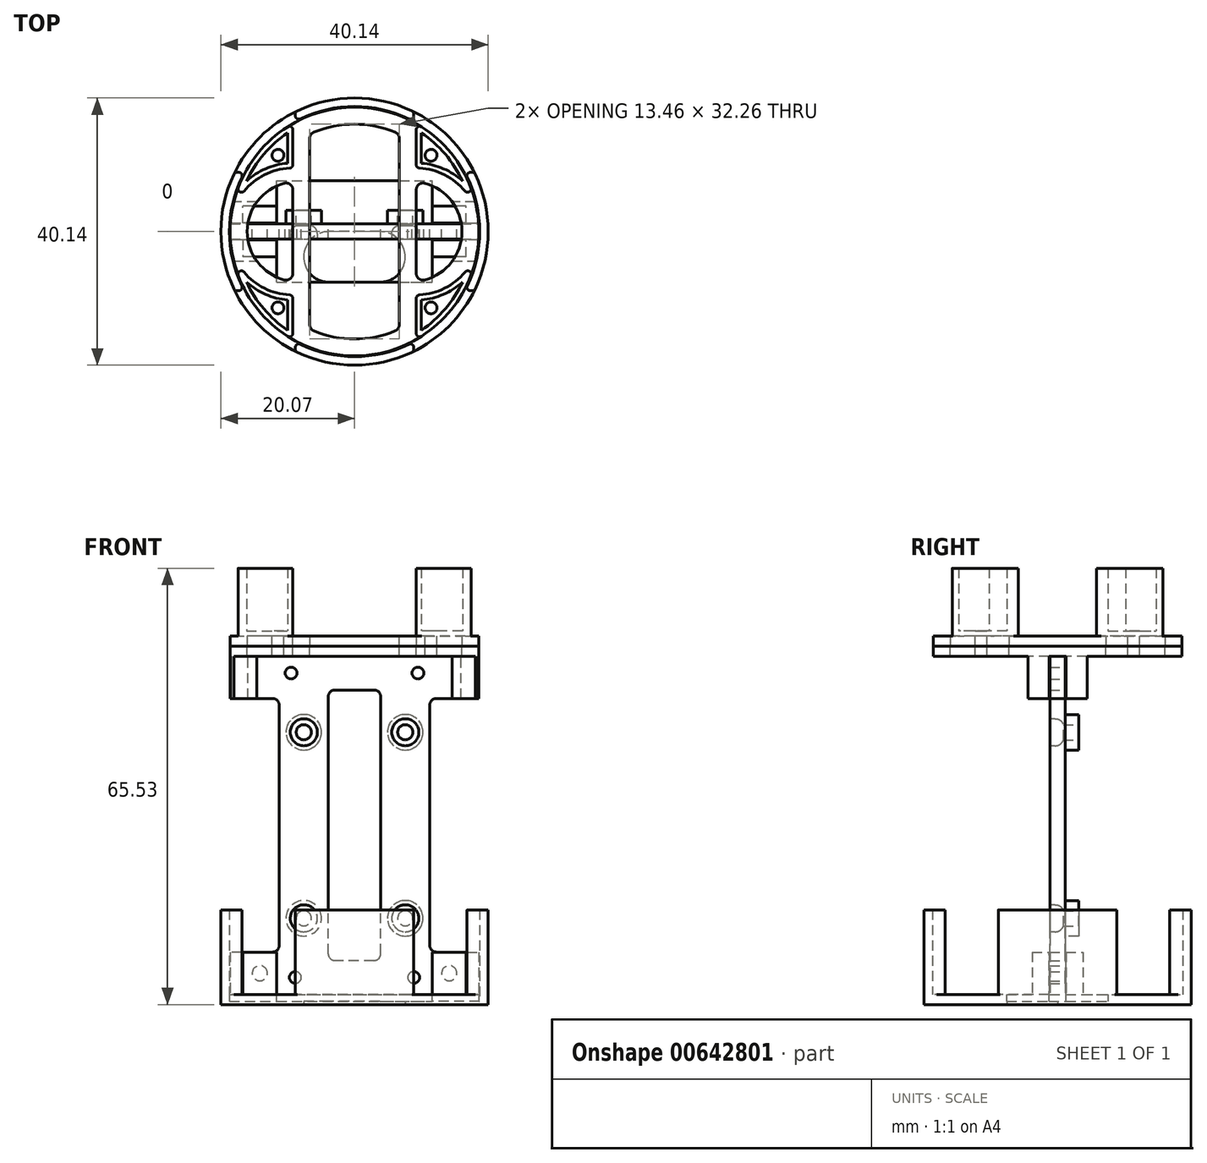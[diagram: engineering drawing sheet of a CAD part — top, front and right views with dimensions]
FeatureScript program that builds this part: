
annotation { "Feature Type Name" : "Feature", "Feature Type Description" : "" }
export const myFeature = defineFeature(function(context is Context, id is Id, definition is map)
    precondition{}
    {
        {
            var Q0;
            Q0=qCreatedBy(makeId("Top.planeOp"),FACE);
            var sketch = newSketch(context, id + "F0", { "sketchPlane" : qUnion([Q0])});
            skCircle(sketch, "E0", {"center": v(0, 0) * mm, "radius": 18.67 * mm});
            skSolve(sketch);
        }
        {
            var Q0;
            Q0=qSketchRegion(id+"F0",true);
            extrude(context, id + "F1", {"entities" : qUnion([Q0]), "depth" : 1.52 * mm, "offsetDistance" : 25.4 * mm});
        }
        {
            var Q0;
            Q0=makeQuery(id+"F1.opExtrude","CAP_FACE",FACE,{"disambiguationData":[OSD([sQuery(id+"F0.wireOp",EDGE,"E0")])],"isStart":false});
            var sketch = newSketch(context, id + "F2", { "sketchPlane" : qUnion([Q0])});
            skLineSegment(sketch, "E1.bottom", {"start": v(-9.27, 9.53) * mm, "end": v(9.27, 9.53) * mm, "construction": true});
            skLineSegment(sketch, "E1.top", {"start": v(-9.27, -9.53) * mm, "end": v(9.27, -9.53) * mm, "construction": true});
            skLineSegment(sketch, "E1.left", {"start": v(-9.27, 9.52) * mm, "end": v(-9.27, -9.53) * mm, "construction": true});
            skLineSegment(sketch, "E1.right", {"start": v(9.27, 9.53) * mm, "end": v(9.27, -9.53) * mm, "construction": true});
            skPoint(sketch, "E1.middle", {"position": v(0, 0) * mm});
            skArc(sketch, "E2", {"start": v(-9.27, 9.52) * mm, "mid": v(-15.18, 7.47) * mm, "end": v(-18.54, 2.2) * mm});
            skArc(sketch, "E3", {"start": v(9.27, -9.52) * mm, "mid": v(15.18, -7.47) * mm, "end": v(18.54, -2.2) * mm});
            skArc(sketch, "E4", {"start": v(-18.54, 2.2) * mm, "mid": v(-18.8, 0) * mm, "end": v(-18.54, -2.2) * mm, "construction": true});
            skArc(sketch, "E5", {"start": v(-18.54, 2.2) * mm, "mid": v(-18.67, 0) * mm, "end": v(-18.54, -2.2) * mm, "construction": true});
            skArc(sketch, "E6", {"start": v(-18.54, -2.2) * mm, "mid": v(0, -18.67) * mm, "end": v(18.54, -2.2) * mm});
            skArc(sketch, "E7", {"start": v(-18.54, -2.2) * mm, "mid": v(-15.18, -7.47) * mm, "end": v(-9.27, -9.53) * mm});
            skArc(sketch, "E8", {"start": v(18.54, 2.2) * mm, "mid": v(15.18, 7.47) * mm, "end": v(9.27, 9.53) * mm});
            skLineSegment(sketch, "E9", {"start": v(18.54, -2.2) * mm, "end": v(18.54, -2.2) * mm});
            skArc(sketch, "E10", {"start": v(18.54, -2.2) * mm, "mid": v(18.8, 0) * mm, "end": v(18.54, 2.2) * mm, "construction": true});
            skLineSegment(sketch, "E11", {"start": v(18.54, 2.2) * mm, "end": v(18.54, 2.2) * mm});
            skArc(sketch, "E12", {"start": v(18.54, 2.2) * mm, "mid": v(0, 18.67) * mm, "end": v(-18.54, 2.2) * mm});
            skArc(sketch, "E13", {"start": v(18.54, -2.2) * mm, "mid": v(18.67, 0) * mm, "end": v(18.54, 2.2) * mm, "construction": true});
            skLineSegment(sketch, "E14", {"start": v(-9.27, -9.53) * mm, "end": v(-9.27, -16.2) * mm});
            skLineSegment(sketch, "E15", {"start": v(9.27, -9.53) * mm, "end": v(9.27, -16.2) * mm});
            skLineSegment(sketch, "E16", {"start": v(9.27, 9.53) * mm, "end": v(9.27, 16.2) * mm});
            skLineSegment(sketch, "E17", {"start": v(-9.27, 9.53) * mm, "end": v(-9.27, 16.2) * mm});
            skArc(sketch, "E18", {"start": v(9.27, 16.2) * mm, "mid": v(0, 18.67) * mm, "end": v(-9.27, 16.2) * mm});
            skArc(sketch, "E19", {"start": v(-9.27, -16.2) * mm, "mid": v(0, -18.67) * mm, "end": v(9.27, -16.2) * mm});
            skSolve(sketch);
        }
        {
            var Q0;
            Q0=qSketchRegion(id+"F2",true);
            extrude(context, id + "F3", {"entities" : qUnion([Q0]), "operationType" : NewBodyOperationType.ADD, "depth" : 10.16 * mm, "offsetDistance" : 25.4 * mm});
        }
        {
            var Q0;
            Q0=makeQuery(id+"F3.opExtrude","SWEPT_EDGE",EDGE,{"disambiguationData":[OSD([sQuery(id+"F0.wireOp",EDGE,"E0"),sQuery(id+"F2.wireOp",EDGE,"E2"),sQuery(id+"F2.wireOp",EDGE,"E12")])]});
            var Q1;
            Q1=makeQuery(id+"F3.opExtrude","SWEPT_EDGE",EDGE,{"disambiguationData":[OSD([sQuery(id+"F0.wireOp",EDGE,"E0"),sQuery(id+"F2.wireOp",EDGE,"E6"),sQuery(id+"F2.wireOp",EDGE,"E7")])]});
            var Q2;
            Q2=makeQuery(id+"F3.opExtrude","SWEPT_EDGE",EDGE,{"disambiguationData":[OSD([sQuery(id+"F0.wireOp",EDGE,"E0"),sQuery(id+"F2.wireOp",EDGE,"E8"),sQuery(id+"F2.wireOp",EDGE,"E12")])]});
            var Q3;
            Q3=makeQuery(id+"F3.opExtrude","SWEPT_EDGE",EDGE,{"disambiguationData":[OSD([sQuery(id+"F0.wireOp",EDGE,"E0"),sQuery(id+"F2.wireOp",EDGE,"E3"),sQuery(id+"F2.wireOp",EDGE,"E6")])]});
            var Q4;
            Q4=makeQuery(id+"F3.opExtrude","SWEPT_EDGE",EDGE,{"disambiguationData":[OSD([sQuery(id+"F2.wireOp",EDGE,"E6"),sQuery(id+"F2.wireOp",EDGE,"E14"),sQuery(id+"F2.wireOp",EDGE,"E19")])]});
            var Q5;
            Q5=makeQuery(id+"F3.opExtrude","SWEPT_EDGE",EDGE,{"disambiguationData":[OSD([sQuery(id+"F0.wireOp",EDGE,"RRU1Pf1V-DoVO-Xhje-gmtz-4FpblWX3eckG.bottom"),sQuery(id+"F0.wireOp",EDGE,"RRU1Pf1V-DoVO-Xhje-gmtz-4FpblWX3eckG.left"),sQuery(id+"F2.wireOp",EDGE,"E7"),sQuery(id+"F2.wireOp",EDGE,"E14")])]});
            var Q6;
            Q6=makeQuery(id+"F3.opExtrude","SWEPT_EDGE",EDGE,{"disambiguationData":[OSD([sQuery(id+"F0.wireOp",EDGE,"RRU1Pf1V-DoVO-Xhje-gmtz-4FpblWX3eckG.top"),sQuery(id+"F0.wireOp",EDGE,"RRU1Pf1V-DoVO-Xhje-gmtz-4FpblWX3eckG.left"),sQuery(id+"F2.wireOp",EDGE,"E2"),sQuery(id+"F2.wireOp",EDGE,"E17")])]});
            var Q7;
            Q7=makeQuery(id+"F3.opExtrude","SWEPT_EDGE",EDGE,{"disambiguationData":[OSD([sQuery(id+"F2.wireOp",EDGE,"E12"),sQuery(id+"F2.wireOp",EDGE,"E17"),sQuery(id+"F2.wireOp",EDGE,"E18")])]});
            var Q8;
            Q8=makeQuery(id+"F3.opExtrude","SWEPT_EDGE",EDGE,{"disambiguationData":[OSD([sQuery(id+"F2.wireOp",EDGE,"E12"),sQuery(id+"F2.wireOp",EDGE,"E16"),sQuery(id+"F2.wireOp",EDGE,"E18")])]});
            var Q9;
            Q9=makeQuery(id+"F3.opExtrude","SWEPT_EDGE",EDGE,{"disambiguationData":[OSD([sQuery(id+"F2.wireOp",EDGE,"E6"),sQuery(id+"F2.wireOp",EDGE,"E15"),sQuery(id+"F2.wireOp",EDGE,"E19")])]});
            var Q10;
            Q10=makeQuery(id+"F3.opExtrude","SWEPT_EDGE",EDGE,{"disambiguationData":[OSD([sQuery(id+"F0.wireOp",EDGE,"RRU1Pf1V-DoVO-Xhje-gmtz-4FpblWX3eckG.top"),sQuery(id+"F0.wireOp",EDGE,"RRU1Pf1V-DoVO-Xhje-gmtz-4FpblWX3eckG.right"),sQuery(id+"F2.wireOp",EDGE,"E8"),sQuery(id+"F2.wireOp",EDGE,"E16")])]});
            var Q11;
            Q11=makeQuery(id+"F3.opExtrude","SWEPT_EDGE",EDGE,{"disambiguationData":[OSD([sQuery(id+"F0.wireOp",EDGE,"RRU1Pf1V-DoVO-Xhje-gmtz-4FpblWX3eckG.bottom"),sQuery(id+"F0.wireOp",EDGE,"RRU1Pf1V-DoVO-Xhje-gmtz-4FpblWX3eckG.right"),sQuery(id+"F2.wireOp",EDGE,"E3"),sQuery(id+"F2.wireOp",EDGE,"E15")])]});
            fillet(context, id + "F4", {"entities" : qUnion([Q0, Q1, Q2, Q3, Q4, Q5, Q6, Q7, Q8, Q9, Q10, Q11]), "radius" : 0.5 * mm, "tangentPropagation" : true, "allowEdgeOverflow" : false});
        }
        {
            var Q0;
            Q0=makeQuery(id+"F3.opExtrude","CAP_FACE",FACE,{"disambiguationData":[OSD([sQuery(id+"F2.wireOp",EDGE,"E1.bottom"),sQuery(id+"F2.wireOp",EDGE,"E2"),sQuery(id+"F2.wireOp",EDGE,"E8"),sQuery(id+"F2.wireOp",EDGE,"E12")])],"isStart":false});
            var Q1;
            Q1=makeQuery(id+"F3.opExtrude","CAP_FACE",FACE,{"disambiguationData":[OSD([sQuery(id+"F2.wireOp",EDGE,"E1.top"),sQuery(id+"F2.wireOp",EDGE,"E3"),sQuery(id+"F2.wireOp",EDGE,"E6"),sQuery(id+"F2.wireOp",EDGE,"E7")])],"isStart":false});
            shell(context, id + "F5", {"entities" : qUnion([Q0, Q1]), "thickness" : 0.76 * mm});
        }
        {
            var Q0;
            Q0=makeQuery(id+"F1.opExtrude","CAP_FACE",FACE,{"disambiguationData":[OSD([sQuery(id+"F0.wireOp",EDGE,"E0")])],"isStart":true});
            var sketch = newSketch(context, id + "F6", { "sketchPlane" : qUnion([Q0])});
            skLineSegment(sketch, "E20.bottom", {"start": v(6.73, -14.66) * mm, "end": v(-6.73, -14.66) * mm, "construction": true});
            skLineSegment(sketch, "E20.top", {"start": v(6.73, 14.66) * mm, "end": v(-6.73, 14.66) * mm, "construction": true});
            skLineSegment(sketch, "E20.left", {"start": v(6.73, -14.66) * mm, "end": v(6.73, 14.66) * mm});
            skLineSegment(sketch, "E20.right", {"start": v(-6.73, -14.66) * mm, "end": v(-6.73, 14.66) * mm});
            skPoint(sketch, "E20.middle", {"position": v(0, 0) * mm});
            skArc(sketch, "E21", {"start": v(-6.73, -14.66) * mm, "mid": v(0, -16.13) * mm, "end": v(6.73, -14.66) * mm});
            skArc(sketch, "E22", {"start": v(6.73, 14.66) * mm, "mid": v(0, 16.13) * mm, "end": v(-6.73, 14.66) * mm});
            skLineSegment(sketch, "E23", {"start": v(0, -16.13) * mm, "end": v(0, -18.67) * mm, "construction": true});
            skLineSegment(sketch, "E24", {"start": v(6.73, -14.66) * mm, "end": v(9.27, -14.66) * mm, "construction": true});
            skLineSegment(sketch, "E25", {"start": v(9.27, -7.48) * mm, "end": v(9.27, 7.48) * mm});
            skPoint(sketch, "E26", {"position": v(9.27, 0) * mm});
            skArc(sketch, "E27", {"start": v(9.27, -7.48) * mm, "mid": v(16.13, 0) * mm, "end": v(9.27, 7.48) * mm});
            skLineSegment(sketch, "E28", {"start": v(16.13, 0) * mm, "end": v(18.67, 0) * mm, "construction": true});
            skLineSegment(sketch, "E29", {"start": v(9.27, -7.48) * mm, "end": v(9.27, -10.02) * mm, "construction": true});
            skLineSegment(sketch, "E30", {"start": v(-9.27, -7.48) * mm, "end": v(-9.27, 7.48) * mm});
            skArc(sketch, "E31", {"start": v(-9.27, 7.48) * mm, "mid": v(-16.13, 0) * mm, "end": v(-9.27, -7.48) * mm});
            skLineSegment(sketch, "E32", {"start": v(-16.13, 0) * mm, "end": v(-18.67, 0) * mm, "construction": true});
            skSolve(sketch);
        }
        {
            var Q0;
            Q0=qSketchRegion(id+"F6",true);
            var Q1;
            Q1=makeQuery(id+"F1.opExtrude","CAP_FACE",FACE,{"disambiguationData":[OSD([sQuery(id+"F0.wireOp",EDGE,"E0")])],"isStart":false});
            extrude(context, id + "F7", {"entities" : qUnion([Q0]), "operationType" : NewBodyOperationType.REMOVE, "endBound" : BoundingType.UP_TO_SURFACE, "oppositeDirection" : true, "depth" : 25.4 * mm, "endBoundEntityFace" : qUnion([Q1]), "offsetDistance" : 25.4 * mm});
        }
        {
            var Q0;
            Q0=makeQuery(id+"F3.opExtrude","CAP_EDGE",EDGE,{"disambiguationData":[OSD([sQuery(id+"F2.wireOp",EDGE,"E2")])],"isStart":true});
            var Q1;
            Q1=makeQuery(id+"F3.opExtrude","CAP_EDGE",EDGE,{"disambiguationData":[OSD([sQuery(id+"F2.wireOp",EDGE,"E7")])],"isStart":true});
            var Q2;
            Q2=makeQuery(id+"F3.opExtrude","CAP_EDGE",EDGE,{"disambiguationData":[OSD([sQuery(id+"F2.wireOp",EDGE,"E3")])],"isStart":true});
            var Q3;
            Q3=makeQuery(id+"F3.opExtrude","CAP_EDGE",EDGE,{"disambiguationData":[OSD([sQuery(id+"F2.wireOp",EDGE,"E8")])],"isStart":true});
            var Q4;
            {var subQ0=sQuery(id+"F6.wireOp",EDGE,"E31");var subQ1=sQuery(id+"F6.wireOp",EDGE,"E30");Q4=makeQuery(id+"F7.boolean.opBoolean","COPY",EDGE,{"derivedFrom":makeQuery(id+"F7.opExtrude","SWEPT_EDGE",EDGE,{"disambiguationData":[OSD([subQ1,subQ0]),TDD([makeQuery(id+"F6.imprint","INTERSECT",VERTEX,{"disambiguationData":[OD(0.0)],"derivedFrom":[subQ1,subQ0]})])]})});}
            var Q5;
            Q5=makeQuery(id+"F7.boolean.opBoolean","COPY",EDGE,{"derivedFrom":makeQuery(id+"F7.opExtrude","SWEPT_EDGE",EDGE,{"disambiguationData":[OSD([sQuery(id+"F6.wireOp",EDGE,"E20.right"),sQuery(id+"F6.wireOp",EDGE,"E21")])]})});
            var Q6;
            Q6=makeQuery(id+"F7.boolean.opBoolean","COPY",EDGE,{"derivedFrom":makeQuery(id+"F7.opExtrude","SWEPT_EDGE",EDGE,{"disambiguationData":[OSD([sQuery(id+"F6.wireOp",EDGE,"E20.left"),sQuery(id+"F6.wireOp",EDGE,"E21")])]})});
            var Q7;
            {var subQ0=sQuery(id+"F6.wireOp",EDGE,"E31");var subQ1=sQuery(id+"F6.wireOp",EDGE,"E30");Q7=makeQuery(id+"F7.boolean.opBoolean","COPY",EDGE,{"derivedFrom":makeQuery(id+"F7.opExtrude","SWEPT_EDGE",EDGE,{"disambiguationData":[OSD([subQ1,subQ0]),TDD([makeQuery(id+"F6.imprint","INTERSECT",VERTEX,{"disambiguationData":[OD(1.0)],"derivedFrom":[subQ1,subQ0]})])]})});}
            var Q8;
            Q8=makeQuery(id+"F7.boolean.opBoolean","COPY",EDGE,{"derivedFrom":makeQuery(id+"F7.opExtrude","SWEPT_EDGE",EDGE,{"disambiguationData":[OSD([sQuery(id+"F6.wireOp",EDGE,"E20.left"),sQuery(id+"F6.wireOp",EDGE,"E22")])]})});
            var Q9;
            {var subQ0=sQuery(id+"F6.wireOp",EDGE,"E27");var subQ1=sQuery(id+"F6.wireOp",EDGE,"E25");Q9=makeQuery(id+"F7.boolean.opBoolean","COPY",EDGE,{"derivedFrom":makeQuery(id+"F7.opExtrude","SWEPT_EDGE",EDGE,{"disambiguationData":[OSD([subQ1,subQ0]),TDD([makeQuery(id+"F6.imprint","INTERSECT",VERTEX,{"disambiguationData":[OD(1.0)],"derivedFrom":[subQ1,subQ0]})])]})});}
            var Q10;
            Q10=makeQuery(id+"F7.boolean.opBoolean","COPY",EDGE,{"derivedFrom":makeQuery(id+"F7.opExtrude","SWEPT_EDGE",EDGE,{"disambiguationData":[OSD([sQuery(id+"F6.wireOp",EDGE,"E20.right"),sQuery(id+"F6.wireOp",EDGE,"E22")])]})});
            var Q11;
            {var subQ0=sQuery(id+"F6.wireOp",EDGE,"E27");var subQ1=sQuery(id+"F6.wireOp",EDGE,"E25");Q11=makeQuery(id+"F7.boolean.opBoolean","COPY",EDGE,{"derivedFrom":makeQuery(id+"F7.opExtrude","SWEPT_EDGE",EDGE,{"disambiguationData":[OSD([subQ1,subQ0]),TDD([makeQuery(id+"F6.imprint","INTERSECT",VERTEX,{"disambiguationData":[OD(0.0)],"derivedFrom":[subQ1,subQ0]})])]})});}
            fillet(context, id + "F8", {"entities" : qUnion([Q0, Q1, Q2, Q3, Q4, Q5, Q6, Q7, Q8, Q9, Q10, Q11]), "radius" : 1.02 * mm, "tangentPropagation" : true, "allowEdgeOverflow" : false});
        }
        {
            var Q0;
            Q0=makeQuery(id+"F5.opShell","OFFSET_FACE",FACE,{"disambiguationData":[OSD([sQuery(id+"F0.wireOp",EDGE,"E0")]),OD(0.0)]});
            var sketch = newSketch(context, id + "F9", { "sketchPlane" : qUnion([Q0])});
            skCircle(sketch, "E33", {"center": v(-11.5, 11.46) * mm, "radius": 0.89 * mm});
            skLineSegment(sketch, "E34.bottom", {"start": v(-11.5, 11.46) * mm, "end": v(11.5, 11.46) * mm, "construction": true});
            skLineSegment(sketch, "E34.top", {"start": v(-11.5, -11.46) * mm, "end": v(11.5, -11.46) * mm, "construction": true});
            skLineSegment(sketch, "E34.left", {"start": v(-11.5, 11.46) * mm, "end": v(-11.5, -11.46) * mm, "construction": true});
            skLineSegment(sketch, "E34.right", {"start": v(11.5, 11.46) * mm, "end": v(11.5, -11.46) * mm, "construction": true});
            skPoint(sketch, "E34.middle", {"position": v(0, 0) * mm});
            skCircle(sketch, "E35", {"center": v(11.5, 11.46) * mm, "radius": 0.89 * mm});
            skCircle(sketch, "E36", {"center": v(11.5, -11.46) * mm, "radius": 0.89 * mm});
            skCircle(sketch, "E37", {"center": v(-11.5, -11.46) * mm, "radius": 0.89 * mm});
            skSolve(sketch);
        }
        {
            var Q0;
            Q0 = qSketchRegion(id + "F9", true);
            var Q1;
            Q1=makeQuery(id+"F1.opExtrude","CAP_FACE",FACE,{"disambiguationData":[OSD([sQuery(id+"F0.wireOp",EDGE,"E0")])],"isStart":true});
            extrude(context, id + "F10", {"entities" : qUnion([Q0]), "operationType" : NewBodyOperationType.REMOVE, "endBound" : BoundingType.UP_TO_SURFACE, "oppositeDirection" : true, "depth" : 25.4 * mm, "endBoundEntityFace" : qUnion([Q1]), "offsetDistance" : 25.4 * mm});
        }
        {
            var Q0;
            Q0=makeQuery(id+"F5.opShell","OFFSET_FACE",FACE,{"disambiguationData":[OSD([sQuery(id+"F0.wireOp",EDGE,"E0")]),OD(2.0)]});
            var Q1;
            Q1=makeQuery(id+"F5.opShell","OFFSET_FACE",FACE,{"disambiguationData":[OSD([sQuery(id+"F0.wireOp",EDGE,"E0")]),OD(1.0)]});
            var Q2;
            Q2=makeQuery(id+"F5.opShell","OFFSET_FACE",FACE,{"disambiguationData":[OSD([sQuery(id+"F0.wireOp",EDGE,"E0")]),OD(3.0)]});
            var Q3;
            Q3=makeQuery(id+"F5.opShell","OFFSET_FACE",FACE,{"disambiguationData":[OSD([sQuery(id+"F0.wireOp",EDGE,"E0")]),OD(0.0)]});
            extrude(context, id + "F11", {"entities" : qUnion([Q0, Q1, Q2, Q3]), "operationType" : NewBodyOperationType.ADD, "depth" : 1.52 * mm, "offsetDistance" : 25.4 * mm});
        }
        {
            var Q0;
            Q0=makeQuery(id+"F1.opExtrude","CAP_FACE",FACE,{"disambiguationData":[OSD([sQuery(id+"F0.wireOp",EDGE,"E0")])],"isStart":true});
            extrude(context, id + "F12", {"entities" : qUnion([Q0]), "depth" : 7.87 * mm, "offsetDistance" : 25.4 * mm});
        }
        {
            var Q0;
            Q0=makeQuery(id+"F12.opExtrude","CAP_FACE",FACE,{"disambiguationData":[OSD([sQuery(id+"F0.wireOp",EDGE,"E0")])],"isStart":false});
            var sketch = newSketch(context, id + "F13", { "sketchPlane" : qUnion([Q0])});
            skArc(sketch, "E38", {"start": v(-18.13, 4.45) * mm, "mid": v(-18.45, 2.87) * mm, "end": v(-18.63, 1.27) * mm, "construction": true});
            skArc(sketch, "E39", {"start": v(-18.13, -4.45) * mm, "mid": v(0, -18.67) * mm, "end": v(18.13, -4.44) * mm});
            skArc(sketch, "E40", {"start": v(18.13, -4.44) * mm, "mid": v(18.45, -2.87) * mm, "end": v(18.63, -1.27) * mm, "construction": true});
            skArc(sketch, "E41", {"start": v(18.13, 4.44) * mm, "mid": v(0, 18.67) * mm, "end": v(-18.13, 4.45) * mm});
            skLineSegment(sketch, "E42", {"start": v(-18.13, 4.45) * mm, "end": v(-9.27, 4.45) * mm});
            skLineSegment(sketch, "E43", {"start": v(18.13, -4.45) * mm, "end": v(9.27, -4.45) * mm});
            skArc(sketch, "E44", {"start": v(-18.63, 1.27) * mm, "mid": v(-18.67, 0) * mm, "end": v(-18.63, -1.27) * mm});
            skArc(sketch, "E45", {"start": v(-18.63, -1.27) * mm, "mid": v(-18.45, -2.87) * mm, "end": v(-18.13, -4.45) * mm, "construction": true});
            skArc(sketch, "E46", {"start": v(18.63, -1.27) * mm, "mid": v(18.67, 0) * mm, "end": v(18.63, 1.27) * mm});
            skArc(sketch, "E47", {"start": v(18.63, 1.27) * mm, "mid": v(18.45, 2.87) * mm, "end": v(18.13, 4.44) * mm, "construction": true});
            skLineSegment(sketch, "E48", {"start": v(18.63, 1.27) * mm, "end": v(9.27, 1.27) * mm});
            skLineSegment(sketch, "E49", {"start": v(-18.63, -1.27) * mm, "end": v(-9.27, -1.27) * mm});
            skLineSegment(sketch, "E50", {"start": v(-9.27, 4.45) * mm, "end": v(9.27, 4.45) * mm, "construction": true});
            skLineSegment(sketch, "E51", {"start": v(-9.27, 1.27) * mm, "end": v(-18.63, 1.27) * mm});
            skLineSegment(sketch, "E52", {"start": v(-9.27, -1.27) * mm, "end": v(9.27, -1.27) * mm, "construction": true});
            skLineSegment(sketch, "E53", {"start": v(-9.27, -4.45) * mm, "end": v(-18.13, -4.45) * mm});
            skLineSegment(sketch, "E54", {"start": v(9.27, -4.45) * mm, "end": v(-9.27, -4.45) * mm, "construction": true});
            skLineSegment(sketch, "E55", {"start": v(9.27, -1.27) * mm, "end": v(18.63, -1.27) * mm});
            skLineSegment(sketch, "E56", {"start": v(9.27, 1.27) * mm, "end": v(-9.27, 1.27) * mm, "construction": true});
            skLineSegment(sketch, "E57", {"start": v(9.27, 4.45) * mm, "end": v(18.13, 4.45) * mm});
            skLineSegment(sketch, "E58", {"start": v(0, 1.27) * mm, "end": v(0, -1.27) * mm, "construction": true});
            skLineSegment(sketch, "E59", {"start": v(0, 4.45) * mm, "end": v(0, -4.45) * mm, "construction": true});
            skLineSegment(sketch, "E60", {"start": v(-9.27, 4.45) * mm, "end": v(-9.27, 1.27) * mm});
            skLineSegment(sketch, "E61", {"start": v(-9.27, -1.27) * mm, "end": v(-9.27, -4.45) * mm});
            skLineSegment(sketch, "E62", {"start": v(9.27, -4.45) * mm, "end": v(9.27, -1.27) * mm});
            skLineSegment(sketch, "E63", {"start": v(9.27, 1.27) * mm, "end": v(9.27, 4.45) * mm});
            skSolve(sketch);
        }
        {
            var Q0;
            Q0 = qSketchRegion(id + "F13", true);
            extrude(context, id + "F14", {"entities" : qUnion([Q0]), "operationType" : NewBodyOperationType.REMOVE, "oppositeDirection" : true, "depth" : 6.35 * mm, "offsetDistance" : 25.4 * mm});
        }
        {
            var Q0;
            Q0=qCreatedBy(makeId("Front.planeOp"),FACE);
            var sketch = newSketch(context, id + "F15", { "sketchPlane" : qUnion([Q0])});
            skLineSegment(sketch, "E64.bottom", {"start": v(-7.62, -40.9) * mm, "end": v(7.62, -40.9) * mm, "construction": true});
            skLineSegment(sketch, "E64.top", {"start": v(-7.62, -12.95) * mm, "end": v(7.62, -12.95) * mm, "construction": true});
            skLineSegment(sketch, "E64.left", {"start": v(-7.62, -40.9) * mm, "end": v(-7.62, -12.95) * mm, "construction": true});
            skLineSegment(sketch, "E64.right", {"start": v(7.62, -40.9) * mm, "end": v(7.62, -12.95) * mm, "construction": true});
            skPoint(sketch, "E64.middle", {"position": v(0, -26.92) * mm});
            skCircle(sketch, "E65", {"center": v(-7.62, -40.9) * mm, "radius": 1.14 * mm});
            skCircle(sketch, "E66", {"center": v(-7.62, -12.95) * mm, "radius": 1.14 * mm});
            skCircle(sketch, "E67", {"center": v(7.62, -12.95) * mm, "radius": 1.14 * mm});
            skCircle(sketch, "E68", {"center": v(7.62, -40.9) * mm, "radius": 1.14 * mm});
            skLineSegment(sketch, "E69", {"start": v(-8.89, -49.78) * mm, "end": v(8.89, -49.78) * mm, "construction": true});
            skLineSegment(sketch, "E70", {"start": v(-9.53, -4.06) * mm, "end": v(9.53, -4.06) * mm, "construction": true});
            skPoint(sketch, "E71", {"position": v(0, -49.78) * mm});
            skPoint(sketch, "E72", {"position": v(0, -4.06) * mm});
            skLineSegment(sketch, "E73", {"start": v(0, -49.78) * mm, "end": v(0, -4.06) * mm, "construction": true});
            skCircle(sketch, "E74", {"center": v(-8.89, -49.78) * mm, "radius": 0.89 * mm});
            skCircle(sketch, "E75", {"center": v(8.89, -49.78) * mm, "radius": 0.89 * mm});
            skCircle(sketch, "E76", {"center": v(9.53, -4.06) * mm, "radius": 0.89 * mm});
            skCircle(sketch, "E77", {"center": v(-9.53, -4.06) * mm, "radius": 0.89 * mm});
            skLineSegment(sketch, "E78", {"start": v(-18.67, -52.32) * mm, "end": v(18.67, -52.32) * mm});
            skPoint(sketch, "E79", {"position": v(0, -52.32) * mm});
            skLineSegment(sketch, "E80", {"start": v(-18.67, -1.52) * mm, "end": v(18.67, -1.52) * mm});
            skLineSegment(sketch, "E81", {"start": v(9.52, -4.06) * mm, "end": v(9.52, -1.52) * mm, "construction": true});
            skLineSegment(sketch, "E82", {"start": v(8.9, -49.78) * mm, "end": v(8.9, -52.32) * mm, "construction": true});
            skLineSegment(sketch, "E83", {"start": v(-18.67, -1.52) * mm, "end": v(-18.67, -7.87) * mm});
            skLineSegment(sketch, "E84", {"start": v(-18.67, -7.87) * mm, "end": v(-11.3, -7.87) * mm});
            skLineSegment(sketch, "E85", {"start": v(-11.3, -7.87) * mm, "end": v(-11.3, -45.97) * mm});
            skLineSegment(sketch, "E86", {"start": v(-11.3, -45.97) * mm, "end": v(-18.67, -45.97) * mm});
            skLineSegment(sketch, "E87", {"start": v(-18.67, -45.97) * mm, "end": v(-18.67, -52.32) * mm});
            skLineSegment(sketch, "E88", {"start": v(18.67, -1.52) * mm, "end": v(18.67, -7.87) * mm});
            skLineSegment(sketch, "E89", {"start": v(18.67, -7.87) * mm, "end": v(11.3, -7.87) * mm});
            skLineSegment(sketch, "E90", {"start": v(11.3, -7.87) * mm, "end": v(11.3, -45.97) * mm});
            skLineSegment(sketch, "E91", {"start": v(11.3, -45.97) * mm, "end": v(18.67, -45.97) * mm});
            skLineSegment(sketch, "E92", {"start": v(18.67, -45.97) * mm, "end": v(18.67, -52.32) * mm});
            skLineSegment(sketch, "E93", {"start": v(-8.76, -40.9) * mm, "end": v(-11.3, -40.9) * mm, "construction": true});
            skLineSegment(sketch, "E94.bottom", {"start": v(3.94, -47.24) * mm, "end": v(-3.94, -47.24) * mm});
            skLineSegment(sketch, "E94.top", {"start": v(3.94, -6.6) * mm, "end": v(-3.94, -6.6) * mm});
            skLineSegment(sketch, "E94.left", {"start": v(3.94, -47.24) * mm, "end": v(3.94, -6.6) * mm});
            skLineSegment(sketch, "E94.right", {"start": v(-3.94, -47.24) * mm, "end": v(-3.94, -6.6) * mm});
            skLineSegment(sketch, "E95", {"start": v(-6.48, -40.9) * mm, "end": v(-3.94, -40.9) * mm, "construction": true});
            skLineSegment(sketch, "E96", {"start": v(0, -49.78) * mm, "end": v(0, -47.24) * mm, "construction": true});
            skCircle(sketch, "E97", {"center": v(-14.22, -49.15) * mm, "radius": 1.14 * mm});
            skPoint(sketch, "E97.centerSnap0", {"position": v(-18.67, -49.15) * mm});
            skCircle(sketch, "E98", {"center": v(14.22, -49.15) * mm, "radius": 1.14 * mm});
            skPoint(sketch, "E98.centerSnap0", {"position": v(18.67, -49.15) * mm});
            skLineSegment(sketch, "E99", {"start": v(-14.22, -49.15) * mm, "end": v(-18.67, -49.15) * mm, "construction": true});
            skLineSegment(sketch, "E100", {"start": v(14.22, -49.15) * mm, "end": v(18.67, -49.15) * mm, "construction": true});
            skSolve(sketch);
        }
        {
            var Q0;
            Q0 = qSketchRegion(id + "F15", true);
            extrude(context, id + "F16", {"entities" : qUnion([Q0]), "endBound" : BoundingType.SYMMETRIC, "depth" : 2.3 * mm, "offsetDistance" : 25.4 * mm});
        }
        {
            var Q0;
            Q0=makeQuery(id+"F16.opExtrude","CAP_FACE",FACE,{"disambiguationData":[OSD([sQuery(id+"F15.wireOp",EDGE,"E65"),sQuery(id+"F15.wireOp",EDGE,"E66"),sQuery(id+"F15.wireOp",EDGE,"E67"),sQuery(id+"F15.wireOp",EDGE,"E68"),sQuery(id+"F15.wireOp",EDGE,"E74"),sQuery(id+"F15.wireOp",EDGE,"E75"),sQuery(id+"F15.wireOp",EDGE,"E76"),sQuery(id+"F15.wireOp",EDGE,"E77"),sQuery(id+"F15.wireOp",EDGE,"E78"),sQuery(id+"F15.wireOp",EDGE,"E80"),sQuery(id+"F15.wireOp",EDGE,"E83"),sQuery(id+"F15.wireOp",EDGE,"E84"),sQuery(id+"F15.wireOp",EDGE,"E85"),sQuery(id+"F15.wireOp",EDGE,"E86"),sQuery(id+"F15.wireOp",EDGE,"E87"),sQuery(id+"F15.wireOp",EDGE,"E88"),sQuery(id+"F15.wireOp",EDGE,"E89"),sQuery(id+"F15.wireOp",EDGE,"E90"),sQuery(id+"F15.wireOp",EDGE,"E91"),sQuery(id+"F15.wireOp",EDGE,"E92"),sQuery(id+"F15.wireOp",EDGE,"E94.bottom"),sQuery(id+"F15.wireOp",EDGE,"E94.top"),sQuery(id+"F15.wireOp",EDGE,"E94.left"),sQuery(id+"F15.wireOp",EDGE,"E94.right")])],"isStart":true});
            var sketch = newSketch(context, id + "F17", { "sketchPlane" : qUnion([Q0])});
            skCircle(sketch, "E101", {"center": v(7.62, -40.9) * mm, "radius": 1.14 * mm});
            skCircle(sketch, "E102", {"center": v(-7.62, -40.9) * mm, "radius": 1.14 * mm});
            skCircle(sketch, "E103", {"center": v(-7.62, -12.95) * mm, "radius": 1.14 * mm});
            skCircle(sketch, "E104", {"center": v(7.62, -12.95) * mm, "radius": 1.14 * mm});
            skCircle(sketch, "E105", {"center": v(7.62, -40.9) * mm, "radius": 2.67 * mm});
            skCircle(sketch, "E106", {"center": v(-7.62, -40.9) * mm, "radius": 2.67 * mm});
            skCircle(sketch, "E107", {"center": v(-7.62, -12.95) * mm, "radius": 2.67 * mm});
            skCircle(sketch, "E108", {"center": v(7.62, -12.95) * mm, "radius": 2.67 * mm});
            skSolve(sketch);
        }
        {
            var Q0;
            Q0 = qSketchRegion(id + "F17", true);
            extrude(context, id + "F18", {"entities" : qUnion([Q0]), "operationType" : NewBodyOperationType.ADD, "depth" : 2.03 * mm, "offsetDistance" : 25.4 * mm});
        }
        {
            var Q0;
            Q0=makeQuery(id+"F18.opExtrude","CAP_EDGE",EDGE,{"disambiguationData":[OSD([sQuery(id+"F17.wireOp",EDGE,"E105")])],"isStart":true});
            var Q1;
            Q1=makeQuery(id+"F18.opExtrude","CAP_EDGE",EDGE,{"disambiguationData":[OSD([sQuery(id+"F17.wireOp",EDGE,"E106")])],"isStart":true});
            var Q2;
            Q2=makeQuery(id+"F18.opExtrude","CAP_EDGE",EDGE,{"disambiguationData":[OSD([sQuery(id+"F17.wireOp",EDGE,"E108")])],"isStart":true});
            var Q3;
            Q3=makeQuery(id+"F18.opExtrude","CAP_EDGE",EDGE,{"disambiguationData":[OSD([sQuery(id+"F17.wireOp",EDGE,"E107")])],"isStart":true});
            var Q4;
            Q4=makeQuery(id+"F16.opExtrude","SWEPT_EDGE",EDGE,{"disambiguationData":[OSD([sQuery(id+"F15.wireOp",EDGE,"E85"),sQuery(id+"F15.wireOp",EDGE,"E86")])]});
            var Q5;
            Q5=makeQuery(id+"F16.opExtrude","SWEPT_EDGE",EDGE,{"disambiguationData":[OSD([sQuery(id+"F15.wireOp",EDGE,"E94.bottom"),sQuery(id+"F15.wireOp",EDGE,"E94.left")])]});
            var Q6;
            Q6=makeQuery(id+"F16.opExtrude","SWEPT_EDGE",EDGE,{"disambiguationData":[OSD([sQuery(id+"F15.wireOp",EDGE,"E94.bottom"),sQuery(id+"F15.wireOp",EDGE,"E94.right")])]});
            var Q7;
            Q7=makeQuery(id+"F16.opExtrude","SWEPT_EDGE",EDGE,{"disambiguationData":[OSD([sQuery(id+"F15.wireOp",EDGE,"E90"),sQuery(id+"F15.wireOp",EDGE,"E91")])]});
            var Q8;
            Q8=makeQuery(id+"F16.opExtrude","SWEPT_EDGE",EDGE,{"disambiguationData":[OSD([sQuery(id+"F15.wireOp",EDGE,"E84"),sQuery(id+"F15.wireOp",EDGE,"E85")])]});
            var Q9;
            Q9=makeQuery(id+"F16.opExtrude","SWEPT_EDGE",EDGE,{"disambiguationData":[OSD([sQuery(id+"F15.wireOp",EDGE,"E94.top"),sQuery(id+"F15.wireOp",EDGE,"E94.left")])]});
            var Q10;
            Q10=makeQuery(id+"F16.opExtrude","SWEPT_EDGE",EDGE,{"disambiguationData":[OSD([sQuery(id+"F15.wireOp",EDGE,"E94.top"),sQuery(id+"F15.wireOp",EDGE,"E94.right")])]});
            var Q11;
            Q11=makeQuery(id+"F16.opExtrude","SWEPT_EDGE",EDGE,{"disambiguationData":[OSD([sQuery(id+"F15.wireOp",EDGE,"E89"),sQuery(id+"F15.wireOp",EDGE,"E90")])]});
            fillet(context, id + "F19", {"entities" : qUnion([Q0, Q1, Q2, Q3, Q4, Q5, Q6, Q7, Q8, Q9, Q10, Q11]), "radius" : 1.02 * mm, "tangentPropagation" : true, "allowEdgeOverflow" : false});
        }
        {
            var Q0;
            Q0=makeQuery(id+"F16.opExtrude","CAP_FACE",FACE,{"disambiguationData":[OSD([sQuery(id+"F15.wireOp",EDGE,"E65"),sQuery(id+"F15.wireOp",EDGE,"E66"),sQuery(id+"F15.wireOp",EDGE,"E67"),sQuery(id+"F15.wireOp",EDGE,"E68"),sQuery(id+"F15.wireOp",EDGE,"E74"),sQuery(id+"F15.wireOp",EDGE,"E75"),sQuery(id+"F15.wireOp",EDGE,"E76"),sQuery(id+"F15.wireOp",EDGE,"E77"),sQuery(id+"F15.wireOp",EDGE,"E78"),sQuery(id+"F15.wireOp",EDGE,"E80"),sQuery(id+"F15.wireOp",EDGE,"E83"),sQuery(id+"F15.wireOp",EDGE,"E84"),sQuery(id+"F15.wireOp",EDGE,"E85"),sQuery(id+"F15.wireOp",EDGE,"E86"),sQuery(id+"F15.wireOp",EDGE,"E87"),sQuery(id+"F15.wireOp",EDGE,"E88"),sQuery(id+"F15.wireOp",EDGE,"E89"),sQuery(id+"F15.wireOp",EDGE,"E90"),sQuery(id+"F15.wireOp",EDGE,"E91"),sQuery(id+"F15.wireOp",EDGE,"E92"),sQuery(id+"F15.wireOp",EDGE,"E94.bottom"),sQuery(id+"F15.wireOp",EDGE,"E94.top"),sQuery(id+"F15.wireOp",EDGE,"E94.left"),sQuery(id+"F15.wireOp",EDGE,"E94.right"),sQuery(id+"F15.wireOp",EDGE,"E97"),sQuery(id+"F15.wireOp",EDGE,"E98")])],"isStart":false});
            var sketch = newSketch(context, id + "F20", { "sketchPlane" : qUnion([Q0])});
            skCircle(sketch, "E109", {"center": v(-7.62, -40.9) * mm, "radius": 2.03 * mm});
            skCircle(sketch, "E110", {"center": v(-7.62, -12.95) * mm, "radius": 2.03 * mm});
            skCircle(sketch, "E111", {"center": v(7.62, -12.95) * mm, "radius": 2.03 * mm});
            skCircle(sketch, "E112", {"center": v(7.62, -40.9) * mm, "radius": 2.03 * mm});
            skSolve(sketch);
        }
        {
            var Q0;
            Q0 = qSketchRegion(id + "F20", true);
            extrude(context, id + "F21", {"entities" : qUnion([Q0]), "operationType" : NewBodyOperationType.REMOVE, "oppositeDirection" : true, "depth" : 2.03 * mm, "offsetDistance" : 25.4 * mm});
        }
        {
            var Q0;
            Q0=makeQuery(id+"F21.boolean.opBoolean","COPY",EDGE,{"derivedFrom":makeQuery(id+"F21.opExtrude","CAP_EDGE",EDGE,{"disambiguationData":[OSD([sQuery(id+"F20.wireOp",EDGE,"E109")])],"isStart":false})});
            var Q1;
            Q1=makeQuery(id+"F21.boolean.opBoolean","COPY",EDGE,{"derivedFrom":makeQuery(id+"F21.opExtrude","CAP_EDGE",EDGE,{"disambiguationData":[OSD([sQuery(id+"F20.wireOp",EDGE,"E110")])],"isStart":false})});
            var Q2;
            Q2=makeQuery(id+"F21.boolean.opBoolean","COPY",EDGE,{"derivedFrom":makeQuery(id+"F21.opExtrude","CAP_EDGE",EDGE,{"disambiguationData":[OSD([sQuery(id+"F20.wireOp",EDGE,"E111")])],"isStart":false})});
            var Q3;
            Q3=makeQuery(id+"F21.boolean.opBoolean","COPY",EDGE,{"derivedFrom":makeQuery(id+"F21.opExtrude","CAP_EDGE",EDGE,{"disambiguationData":[OSD([sQuery(id+"F20.wireOp",EDGE,"E112")])],"isStart":false})});
            fillet(context, id + "F22", {"entities" : qUnion([Q0, Q1, Q2, Q3]), "radius" : 1.27 * mm, "tangentPropagation" : true, "allowEdgeOverflow" : false});
        }
        {
            var Q0;
            Q0=makeQuery(id+"F16.opExtrude","SWEPT_FACE",FACE,{"disambiguationData":[OSD([sQuery(id+"F15.wireOp",EDGE,"E78")])]});
            var sketch = newSketch(context, id + "F23", { "sketchPlane" : qUnion([Q0])});
            skCircle(sketch, "E113", {"center": v(0, 0) * mm, "radius": 20.07 * mm});
            skSolve(sketch);
        }
        {
            var Q0;
            Q0 = qSketchRegion(id + "F23", true);
            extrude(context, id + "F24", {"entities" : qUnion([Q0]), "depth" : 1.52 * mm, "offsetDistance" : 25.4 * mm});
        }
        {
            var Q0;
            Q0=makeQuery(id+"F24.opExtrude","CAP_FACE",FACE,{"disambiguationData":[OSD([sQuery(id+"F23.wireOp",EDGE,"E113")])],"isStart":false});
            var sketch = newSketch(context, id + "F25", { "sketchPlane" : qUnion([Q0])});
            skLineSegment(sketch, "E114.bottom", {"start": v(3.8, 0) * mm, "end": v(-3.8, 0) * mm});
            skLineSegment(sketch, "E114.top", {"start": v(3.8, 7.62) * mm, "end": v(-3.8, 7.62) * mm});
            skLineSegment(sketch, "E114.left", {"start": v(3.8, 0) * mm, "end": v(3.8, 7.62) * mm});
            skLineSegment(sketch, "E114.right", {"start": v(-3.81, 0) * mm, "end": v(-3.81, 7.62) * mm});
            skArc(sketch, "E115", {"start": v(3.81, 0) * mm, "mid": v(7.62, 3.81) * mm, "end": v(3.8, 7.62) * mm});
            skArc(sketch, "E116", {"start": v(-3.81, 7.62) * mm, "mid": v(-7.62, 3.81) * mm, "end": v(-3.81, 0) * mm});
            skPoint(sketch, "E117", {"position": v(0, 0) * mm});
            skSolve(sketch);
        }
        {
            var Q0;
            Q0 = qSketchRegion(id + "F25", true);
            var Q1;
            Q1=makeQuery(id+"F24.opExtrude","CAP_FACE",FACE,{"disambiguationData":[OSD([sQuery(id+"F23.wireOp",EDGE,"E113")])],"isStart":true});
            extrude(context, id + "F26", {"entities" : qUnion([Q0]), "operationType" : NewBodyOperationType.REMOVE, "endBound" : BoundingType.UP_TO_SURFACE, "oppositeDirection" : true, "depth" : 25.4 * mm, "endBoundEntityFace" : qUnion([Q1]), "offsetDistance" : 25.4 * mm});
        }
        {
            var Q0;
            Q0=makeQuery(id+"F24.opExtrude","CAP_FACE",FACE,{"disambiguationData":[OSD([sQuery(id+"F23.wireOp",EDGE,"E113")])],"isStart":true});
            var sketch = newSketch(context, id + "F27", { "sketchPlane" : qUnion([Q0])});
            skLineSegment(sketch, "E118.bottom", {"start": v(16.76, -3.8) * mm, "end": v(11.68, -3.81) * mm});
            skLineSegment(sketch, "E118.top", {"start": v(16.76, -1.27) * mm, "end": v(11.68, -1.27) * mm});
            skLineSegment(sketch, "E118.left", {"start": v(16.76, -3.81) * mm, "end": v(16.76, -1.27) * mm});
            skLineSegment(sketch, "E118.right", {"start": v(11.68, -3.8) * mm, "end": v(11.68, -1.27) * mm});
            skLineSegment(sketch, "E119.bottom", {"start": v(-11.68, 1.27) * mm, "end": v(-16.76, 1.27) * mm});
            skLineSegment(sketch, "E119.top", {"start": v(-11.68, 3.81) * mm, "end": v(-16.76, 3.81) * mm});
            skLineSegment(sketch, "E119.left", {"start": v(-11.68, 1.27) * mm, "end": v(-11.68, 3.81) * mm});
            skLineSegment(sketch, "E119.right", {"start": v(-16.76, 1.27) * mm, "end": v(-16.76, 3.81) * mm});
            skPoint(sketch, "E120", {"position": v(-14.22, 1.27) * mm});
            skPoint(sketch, "E121", {"position": v(-18.67, 1.14) * mm});
            skPoint(sketch, "E122", {"position": v(-20.07, 0) * mm});
            skPoint(sketch, "E123", {"position": v(20.07, 0) * mm});
            skPoint(sketch, "E124", {"position": v(18.67, -1.14) * mm});
            skPoint(sketch, "E125", {"position": v(14.22, -1.27) * mm});
            skLineSegment(sketch, "E126.bottom", {"start": v(16.76, 1.27) * mm, "end": v(11.68, 1.27) * mm});
            skLineSegment(sketch, "E126.top", {"start": v(16.76, 3.81) * mm, "end": v(11.68, 3.81) * mm});
            skLineSegment(sketch, "E126.left", {"start": v(16.76, 1.27) * mm, "end": v(16.76, 3.81) * mm});
            skLineSegment(sketch, "E126.right", {"start": v(11.68, 1.27) * mm, "end": v(11.68, 3.81) * mm});
            skLineSegment(sketch, "E127.bottom", {"start": v(-11.68, -1.27) * mm, "end": v(-16.76, -1.27) * mm});
            skLineSegment(sketch, "E127.top", {"start": v(-11.68, -3.8) * mm, "end": v(-16.76, -3.81) * mm});
            skLineSegment(sketch, "E127.left", {"start": v(-11.68, -1.27) * mm, "end": v(-11.68, -3.81) * mm});
            skLineSegment(sketch, "E127.right", {"start": v(-16.76, -1.27) * mm, "end": v(-16.76, -3.8) * mm});
            skSolve(sketch);
        }
        {
            var Q0;
            Q0=makeQuery(id+"F24.opExtrude","CAP_FACE",FACE,{"disambiguationData":[OSD([sQuery(id+"F23.wireOp",EDGE,"E113")])],"isStart":true});
            var sketch = newSketch(context, id + "F28", { "sketchPlane" : qUnion([Q0])});
            skLineSegment(sketch, "E128", {"start": v(0, -18.8) * mm, "end": v(0, -20.07) * mm, "construction": true});
            skArc(sketch, "E129", {"start": v(8.89, 17.99) * mm, "mid": v(0, 20.07) * mm, "end": v(-8.89, 17.99) * mm});
            skArc(sketch, "E130", {"start": v(-8.89, 17.99) * mm, "mid": v(-14.19, 14.19) * mm, "end": v(-17.99, 8.89) * mm, "construction": true});
            skArc(sketch, "E131", {"start": v(-8.9, 16.56) * mm, "mid": v(-13.3, 13.3) * mm, "end": v(-16.56, 8.89) * mm, "construction": true});
            skArc(sketch, "E132", {"start": v(8.9, 16.56) * mm, "mid": v(0, 18.8) * mm, "end": v(-8.9, 16.56) * mm});
            skArc(sketch, "E133", {"start": v(-8.9, -16.56) * mm, "mid": v(0, -18.8) * mm, "end": v(8.9, -16.56) * mm});
            skArc(sketch, "E134", {"start": v(8.9, -16.56) * mm, "mid": v(13.3, -13.3) * mm, "end": v(16.56, -8.89) * mm, "construction": true});
            skArc(sketch, "E135", {"start": v(8.89, -17.99) * mm, "mid": v(14.19, -14.19) * mm, "end": v(17.99, -8.89) * mm, "construction": true});
            skArc(sketch, "E136", {"start": v(-8.89, -17.99) * mm, "mid": v(0, -20.07) * mm, "end": v(8.89, -17.99) * mm});
            skLineSegment(sketch, "E137", {"start": v(8.89, 16.56) * mm, "end": v(8.89, 17.99) * mm});
            skLineSegment(sketch, "E138", {"start": v(-8.9, 17.99) * mm, "end": v(-8.9, 16.56) * mm});
            skLineSegment(sketch, "E139", {"start": v(-8.89, -16.56) * mm, "end": v(-8.89, -17.99) * mm});
            skLineSegment(sketch, "E140", {"start": v(8.89, -16.56) * mm, "end": v(8.9, -17.99) * mm});
            skArc(sketch, "E141", {"start": v(16.56, 8.89) * mm, "mid": v(13.3, 13.3) * mm, "end": v(8.9, 16.56) * mm, "construction": true});
            skArc(sketch, "E142", {"start": v(17.99, 8.89) * mm, "mid": v(14.19, 14.19) * mm, "end": v(8.89, 17.99) * mm, "construction": true});
            skArc(sketch, "E143", {"start": v(16.56, -8.89) * mm, "mid": v(18.8, 0) * mm, "end": v(16.56, 8.89) * mm});
            skArc(sketch, "E144", {"start": v(17.99, -8.89) * mm, "mid": v(20.07, 0) * mm, "end": v(17.99, 8.89) * mm});
            skArc(sketch, "E145", {"start": v(-16.56, 8.89) * mm, "mid": v(-18.8, 0) * mm, "end": v(-16.56, -8.89) * mm});
            skArc(sketch, "E146", {"start": v(-17.99, 8.89) * mm, "mid": v(-20.07, 0) * mm, "end": v(-17.99, -8.89) * mm});
            skArc(sketch, "E147", {"start": v(-16.56, -8.89) * mm, "mid": v(-13.3, -13.3) * mm, "end": v(-8.9, -16.56) * mm, "construction": true});
            skArc(sketch, "E148", {"start": v(-17.99, -8.89) * mm, "mid": v(-14.19, -14.19) * mm, "end": v(-8.89, -17.99) * mm, "construction": true});
            skLineSegment(sketch, "E149", {"start": v(-16.56, -8.9) * mm, "end": v(-17.99, -8.9) * mm});
            skLineSegment(sketch, "E150", {"start": v(-16.56, 8.89) * mm, "end": v(-17.99, 8.89) * mm});
            skLineSegment(sketch, "E151", {"start": v(17.99, 8.9) * mm, "end": v(16.56, 8.9) * mm});
            skLineSegment(sketch, "E152", {"start": v(17.99, -8.9) * mm, "end": v(16.56, -8.9) * mm});
            skSolve(sketch);
        }
        {
            var Q0;
            Q0 = qSketchRegion(id + "F28", true);
            extrude(context, id + "F29", {"entities" : qUnion([Q0]), "operationType" : NewBodyOperationType.ADD, "depth" : 12.7 * mm, "offsetDistance" : 25.4 * mm});
        }
        {
            var Q0;
            Q0=makeQuery(id+"F29.opExtrude","SWEPT_EDGE",EDGE,{"disambiguationData":[OSD([sQuery(id+"F23.wireOp",EDGE,"E113"),sQuery(id+"F28.wireOp",EDGE,"E146"),sQuery(id+"F28.wireOp",EDGE,"E149")])]});
            var Q1;
            Q1=makeQuery(id+"F29.opExtrude","SWEPT_EDGE",EDGE,{"disambiguationData":[OSD([sQuery(id+"F28.wireOp",EDGE,"E145"),sQuery(id+"F28.wireOp",EDGE,"E149")])]});
            var Q2;
            Q2=makeQuery(id+"F29.opExtrude","SWEPT_EDGE",EDGE,{"disambiguationData":[OSD([sQuery(id+"F23.wireOp",EDGE,"E113"),sQuery(id+"F28.wireOp",EDGE,"E146"),sQuery(id+"F28.wireOp",EDGE,"E150")])]});
            var Q3;
            Q3=makeQuery(id+"F29.opExtrude","SWEPT_EDGE",EDGE,{"disambiguationData":[OSD([sQuery(id+"F28.wireOp",EDGE,"E145"),sQuery(id+"F28.wireOp",EDGE,"E150")])]});
            var Q4;
            Q4=makeQuery(id+"F29.opExtrude","SWEPT_EDGE",EDGE,{"disambiguationData":[OSD([sQuery(id+"F23.wireOp",EDGE,"E113"),sQuery(id+"F28.wireOp",EDGE,"E129"),sQuery(id+"F28.wireOp",EDGE,"E138")])]});
            var Q5;
            Q5=makeQuery(id+"F29.opExtrude","SWEPT_EDGE",EDGE,{"disambiguationData":[OSD([sQuery(id+"F28.wireOp",EDGE,"E132"),sQuery(id+"F28.wireOp",EDGE,"E138")])]});
            var Q6;
            Q6=makeQuery(id+"F29.opExtrude","SWEPT_EDGE",EDGE,{"disambiguationData":[OSD([sQuery(id+"F23.wireOp",EDGE,"E113"),sQuery(id+"F28.wireOp",EDGE,"E129"),sQuery(id+"F28.wireOp",EDGE,"E137")])]});
            var Q7;
            Q7=makeQuery(id+"F29.opExtrude","SWEPT_EDGE",EDGE,{"disambiguationData":[OSD([sQuery(id+"F28.wireOp",EDGE,"E143"),sQuery(id+"F28.wireOp",EDGE,"E151")])]});
            var Q8;
            Q8=makeQuery(id+"F29.opExtrude","SWEPT_EDGE",EDGE,{"disambiguationData":[OSD([sQuery(id+"F28.wireOp",EDGE,"E132"),sQuery(id+"F28.wireOp",EDGE,"E137")])]});
            var Q9;
            Q9=makeQuery(id+"F29.opExtrude","SWEPT_EDGE",EDGE,{"disambiguationData":[OSD([sQuery(id+"F28.wireOp",EDGE,"E133"),sQuery(id+"F28.wireOp",EDGE,"E139")])]});
            var Q10;
            Q10=makeQuery(id+"F29.opExtrude","SWEPT_EDGE",EDGE,{"disambiguationData":[OSD([sQuery(id+"F23.wireOp",EDGE,"E113"),sQuery(id+"F28.wireOp",EDGE,"E144"),sQuery(id+"F28.wireOp",EDGE,"E152")])]});
            var Q11;
            Q11=makeQuery(id+"F29.opExtrude","SWEPT_EDGE",EDGE,{"disambiguationData":[OSD([sQuery(id+"F28.wireOp",EDGE,"E133"),sQuery(id+"F28.wireOp",EDGE,"E140")])]});
            var Q12;
            Q12=makeQuery(id+"F29.opExtrude","SWEPT_EDGE",EDGE,{"disambiguationData":[OSD([sQuery(id+"F23.wireOp",EDGE,"E113"),sQuery(id+"F28.wireOp",EDGE,"E136"),sQuery(id+"F28.wireOp",EDGE,"E140")])]});
            var Q13;
            Q13=makeQuery(id+"F29.opExtrude","SWEPT_EDGE",EDGE,{"disambiguationData":[OSD([sQuery(id+"F28.wireOp",EDGE,"E143"),sQuery(id+"F28.wireOp",EDGE,"E152")])]});
            var Q14;
            Q14=makeQuery(id+"F29.opExtrude","SWEPT_EDGE",EDGE,{"disambiguationData":[OSD([sQuery(id+"F23.wireOp",EDGE,"E113"),sQuery(id+"F28.wireOp",EDGE,"E136"),sQuery(id+"F28.wireOp",EDGE,"E139")])]});
            var Q15;
            Q15=makeQuery(id+"F9CcIupZvPesqnZ_4.opExtrude","CAP_EDGE",EDGE,{"disambiguationData":[OSD([sQuery(id+"F27.wireOp",EDGE,"E119.top")])],"isStart":true});
            var Q16;
            Q16=makeQuery(id+"F9CcIupZvPesqnZ_4.opExtrude","CAP_EDGE",EDGE,{"disambiguationData":[OSD([sQuery(id+"F27.wireOp",EDGE,"E119.left")])],"isStart":true});
            var Q17;
            Q17=makeQuery(id+"F9CcIupZvPesqnZ_4.opExtrude","CAP_EDGE",EDGE,{"disambiguationData":[OSD([sQuery(id+"F27.wireOp",EDGE,"E119.right")])],"isStart":true});
            var Q18;
            Q18=makeQuery(id+"F9CcIupZvPesqnZ_4.opExtrude","CAP_EDGE",EDGE,{"disambiguationData":[OSD([sQuery(id+"F27.wireOp",EDGE,"E118.bottom")])],"isStart":true});
            var Q19;
            Q19=makeQuery(id+"F9CcIupZvPesqnZ_4.opExtrude","CAP_EDGE",EDGE,{"disambiguationData":[OSD([sQuery(id+"F27.wireOp",EDGE,"E118.right")])],"isStart":true});
            var Q20;
            Q20=makeQuery(id+"F9CcIupZvPesqnZ_4.opExtrude","CAP_EDGE",EDGE,{"disambiguationData":[OSD([sQuery(id+"F27.wireOp",EDGE,"E118.left")])],"isStart":true});
            var Q21;
            Q21=makeQuery(id+"FTdqqJJ1uaoRHuZ_4.boolean.opBoolean","COPY",EDGE,{"derivedFrom":makeQuery(id+"FTdqqJJ1uaoRHuZ_4.opExtrude","CAP_EDGE",EDGE,{"disambiguationData":[OSD([sQuery(id+"FRstoslxKUlpYfS_4.wireOp",EDGE,"NezGoiiS-aYT4-GAeU-ITZW-Vp81R6vTZ9WE")])],"isStart":true})});
            var Q22;
            Q22=makeQuery(id+"FbMhszmMvsPUCB8_4.boolean.opBoolean","COPY",EDGE,{"derivedFrom":makeQuery(id+"FbMhszmMvsPUCB8_4.opExtrude","CAP_EDGE",EDGE,{"disambiguationData":[OSD([sQuery(id+"FipGp7p7evltkC6_4.wireOp",EDGE,"wkVAbJIZ-Wn6U-QkLl-WT0G-faB8G608tSpa")])],"isStart":true})});
            var Q23;
            Q23=makeQuery(id+"F29.opExtrude","SWEPT_EDGE",EDGE,{"disambiguationData":[OSD([sQuery(id+"F23.wireOp",EDGE,"E113"),sQuery(id+"F28.wireOp",EDGE,"E144"),sQuery(id+"F28.wireOp",EDGE,"E151")])]});
            var Q24;
            Q24=makeQuery(id+"F9CcIupZvPesqnZ_4.opExtrude","SWEPT_EDGE",EDGE,{"disambiguationData":[OSD([sQuery(id+"F27.wireOp",EDGE,"E118.bottom"),sQuery(id+"F27.wireOp",EDGE,"E118.right")])]});
            var Q25;
            Q25=makeQuery(id+"F9CcIupZvPesqnZ_4.opExtrude","SWEPT_EDGE",EDGE,{"disambiguationData":[OSD([sQuery(id+"F27.wireOp",EDGE,"E118.bottom"),sQuery(id+"F27.wireOp",EDGE,"E118.left")])]});
            var Q26;
            Q26=makeQuery(id+"F9CcIupZvPesqnZ_4.opExtrude","SWEPT_EDGE",EDGE,{"disambiguationData":[OSD([sQuery(id+"F27.wireOp",EDGE,"E119.top"),sQuery(id+"F27.wireOp",EDGE,"E119.left")])]});
            var Q27;
            Q27=makeQuery(id+"F9CcIupZvPesqnZ_4.opExtrude","SWEPT_EDGE",EDGE,{"disambiguationData":[OSD([sQuery(id+"F27.wireOp",EDGE,"E119.top"),sQuery(id+"F27.wireOp",EDGE,"E119.right")])]});
            var Q28;
            Q28=makeQuery(id+"F9CcIupZvPesqnZ_4.opExtrude","TWEAK_EDGE",EDGE,{"derivedFrom":[makeQuery(id+"F16.opExtrude","SWEPT_FACE",FACE,{"disambiguationData":[OSD([sQuery(id+"F15.wireOp",EDGE,"E91")])]}),makeQuery(id+"F27.imprint","IMPRINT",EDGE,{"derivedFrom":sQuery(id+"F27.wireOp",EDGE,"E118.bottom")})]});
            var Q29;
            Q29=makeQuery(id+"F9CcIupZvPesqnZ_4.opExtrude","TWEAK_EDGE",EDGE,{"derivedFrom":[makeQuery(id+"F16.opExtrude","SWEPT_FACE",FACE,{"disambiguationData":[OSD([sQuery(id+"F15.wireOp",EDGE,"E91")])]}),makeQuery(id+"F27.imprint","IMPRINT",EDGE,{"derivedFrom":sQuery(id+"F27.wireOp",EDGE,"E118.left")})]});
            var Q30;
            Q30=makeQuery(id+"F9CcIupZvPesqnZ_4.opExtrude","TWEAK_EDGE",EDGE,{"derivedFrom":[makeQuery(id+"F16.opExtrude","SWEPT_FACE",FACE,{"disambiguationData":[OSD([sQuery(id+"F15.wireOp",EDGE,"E91")])]}),makeQuery(id+"F27.imprint","IMPRINT",EDGE,{"derivedFrom":sQuery(id+"F27.wireOp",EDGE,"E118.right")})]});
            var Q31;
            Q31=makeQuery(id+"F9CcIupZvPesqnZ_4.opExtrude","TWEAK_EDGE",EDGE,{"derivedFrom":[makeQuery(id+"F16.opExtrude","SWEPT_FACE",FACE,{"disambiguationData":[OSD([sQuery(id+"F15.wireOp",EDGE,"E91")])]}),makeQuery(id+"F27.imprint","IMPRINT",EDGE,{"derivedFrom":sQuery(id+"F27.wireOp",EDGE,"E119.left")})]});
            var Q32;
            Q32=makeQuery(id+"F9CcIupZvPesqnZ_4.opExtrude","TWEAK_EDGE",EDGE,{"derivedFrom":[makeQuery(id+"F16.opExtrude","SWEPT_FACE",FACE,{"disambiguationData":[OSD([sQuery(id+"F15.wireOp",EDGE,"E91")])]}),makeQuery(id+"F27.imprint","IMPRINT",EDGE,{"derivedFrom":sQuery(id+"F27.wireOp",EDGE,"E119.top")})]});
            var Q33;
            Q33=makeQuery(id+"F9CcIupZvPesqnZ_4.opExtrude","TWEAK_EDGE",EDGE,{"derivedFrom":[makeQuery(id+"F16.opExtrude","SWEPT_FACE",FACE,{"disambiguationData":[OSD([sQuery(id+"F15.wireOp",EDGE,"E91")])]}),makeQuery(id+"F27.imprint","IMPRINT",EDGE,{"derivedFrom":sQuery(id+"F27.wireOp",EDGE,"E119.right")})]});
            fillet(context, id + "F30", {"entities" : qUnion([Q0, Q1, Q2, Q3, Q4, Q5, Q6, Q7, Q8, Q9, Q10, Q11, Q12, Q13, Q14, Q15, Q16, Q17, Q18, Q19, Q20, Q21, Q22, Q23, Q24, Q25, Q26, Q27, Q28, Q29, Q30, Q31, Q32, Q33]), "radius" : 0.5 * mm, "tangentPropagation" : true, "allowEdgeOverflow" : false});
        }
        {
            var Q0;
            Q0=makeQuery(id+"F24.opExtrude","CAP_FACE",FACE,{"disambiguationData":[OSD([sQuery(id+"F23.wireOp",EDGE,"E113")])],"isStart":true});
            var sketch = newSketch(context, id + "F31", { "sketchPlane" : qUnion([Q0])});
            skLineSegment(sketch, "E153", {"start": v(-18.75, 1.27) * mm, "end": v(-11.68, 1.27) * mm});
            skLineSegment(sketch, "E154", {"start": v(18.75, -1.27) * mm, "end": v(11.68, -1.27) * mm});
            skArc(sketch, "E155", {"start": v(18.75, -1.27) * mm, "mid": v(18.8, 0) * mm, "end": v(18.75, 1.27) * mm});
            skArc(sketch, "E156", {"start": v(-18.75, 1.27) * mm, "mid": v(-18.8, 0) * mm, "end": v(-18.75, -1.27) * mm});
            skPoint(sketch, "E157", {"position": v(-18.8, 0) * mm});
            skLineSegment(sketch, "E158.bottom", {"start": v(-11.68, -7.62) * mm, "end": v(11.68, -7.62) * mm});
            skLineSegment(sketch, "E158.top", {"start": v(-11.68, 7.62) * mm, "end": v(11.68, 7.62) * mm});
            skLineSegment(sketch, "E158.left", {"start": v(-11.68, -7.62) * mm, "end": v(-11.68, -1.27) * mm});
            skLineSegment(sketch, "E158.right", {"start": v(11.68, -7.62) * mm, "end": v(11.68, -1.27) * mm});
            skLineSegment(sketch, "E159", {"start": v(11.68, -1.27) * mm, "end": v(11.68, 1.27) * mm, "construction": true});
            skLineSegment(sketch, "E160", {"start": v(11.68, 1.27) * mm, "end": v(11.68, 7.62) * mm});
            skLineSegment(sketch, "E161", {"start": v(11.68, 1.27) * mm, "end": v(18.75, 1.27) * mm});
            skLineSegment(sketch, "E162", {"start": v(11.68, -1.27) * mm, "end": v(11.68, -1.27) * mm});
            skLineSegment(sketch, "E163", {"start": v(-11.68, -1.27) * mm, "end": v(-11.68, 1.27) * mm, "construction": true});
            skLineSegment(sketch, "E164", {"start": v(-11.68, -1.27) * mm, "end": v(-18.75, -1.27) * mm});
            skLineSegment(sketch, "E165", {"start": v(-11.68, 1.27) * mm, "end": v(11.68, 1.27) * mm, "construction": true});
            skLineSegment(sketch, "E166", {"start": v(-11.68, 1.27) * mm, "end": v(-11.68, 7.62) * mm});
            skLineSegment(sketch, "E167", {"start": v(11.68, -1.27) * mm, "end": v(-11.68, -1.27) * mm, "construction": true});
            skSolve(sketch);
        }
        {
            var Q0;
            Q0 = qSketchRegion(id + "F31", true);
            extrude(context, id + "F32", {"entities" : qUnion([Q0]), "operationType" : NewBodyOperationType.REMOVE, "oppositeDirection" : true, "depth" : 1.02 * mm, "offsetDistance" : 25.4 * mm});
        }
        {
            var Q0;
            Q0 = qSketchRegion(id + "F27", true);
            extrude(context, id + "F33", {"entities" : qUnion([Q0]), "operationType" : NewBodyOperationType.ADD, "depth" : 6.35 * mm, "offsetDistance" : 25.4 * mm});
        }
    });
